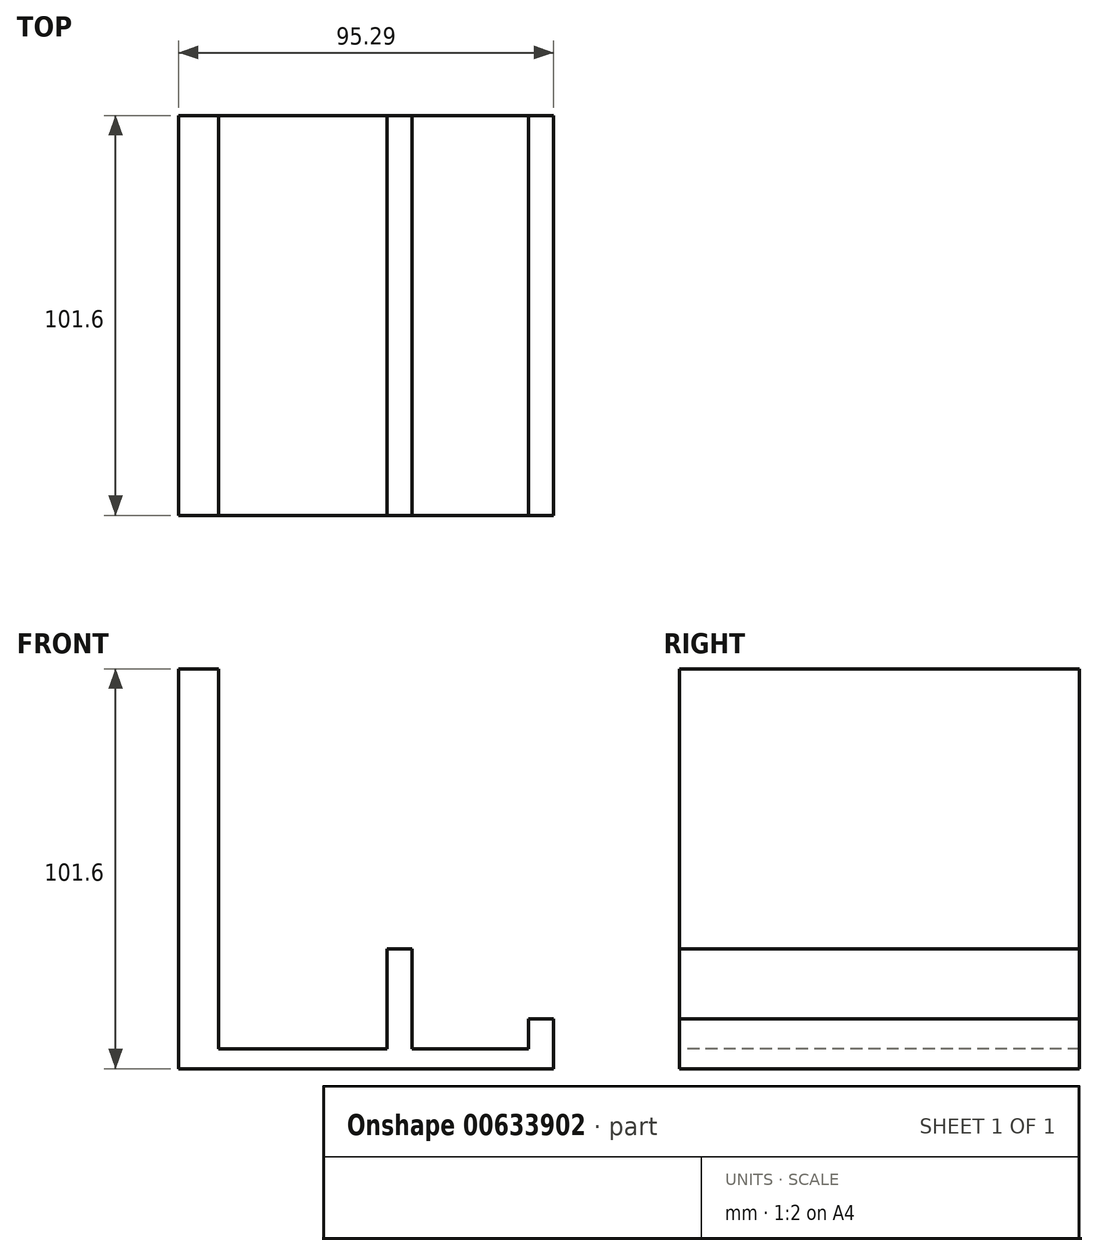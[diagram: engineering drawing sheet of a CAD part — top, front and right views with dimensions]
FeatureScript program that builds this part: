
annotation { "Feature Type Name" : "Feature", "Feature Type Description" : "" }
export const myFeature = defineFeature(function(context is Context, id is Id, definition is map)
    precondition{}
    {
        {
            var Q0;
            Q0=qCreatedBy(makeId("Front.planeOp"),FACE);
            var sketch = newSketch(context, id + "F0", { "sketchPlane" : qUnion([Q0])});
            skLineSegment(sketch, "E0", {"start": v(-57.6, 53.74) * mm, "end": v(-57.6, -47.86) * mm});
            skLineSegment(sketch, "E1", {"start": v(1.68, -42.78) * mm, "end": v(-47.46, -42.78) * mm});
            skLineSegment(sketch, "E2", {"start": v(-47.46, -42.78) * mm, "end": v(-47.46, 53.74) * mm});
            skLineSegment(sketch, "E3", {"start": v(-47.46, 53.74) * mm, "end": v(-57.6, 53.74) * mm});
            skLineSegment(sketch, "E4", {"start": v(-4.67, -42.78) * mm, "end": v(-4.67, -17.38) * mm});
            skLineSegment(sketch, "E5", {"start": v(-4.67, -17.38) * mm, "end": v(1.68, -17.38) * mm});
            skLineSegment(sketch, "E6", {"start": v(1.68, -17.38) * mm, "end": v(1.68, -42.78) * mm});
            skLineSegment(sketch, "E7", {"start": v(-57.6, -47.86) * mm, "end": v(37.7, -47.86) * mm});
            skLineSegment(sketch, "E8", {"start": v(37.7, -47.86) * mm, "end": v(37.7, -35.16) * mm});
            skLineSegment(sketch, "E9", {"start": v(37.7, -35.16) * mm, "end": v(31.34, -35.16) * mm});
            skLineSegment(sketch, "E10", {"start": v(31.34, -35.16) * mm, "end": v(31.34, -42.78) * mm});
            skLineSegment(sketch, "E11", {"start": v(31.34, -42.78) * mm, "end": v(1.68, -42.78) * mm});
            skSolve(sketch);
        }
        {
            var Q0;
            Q0=makeQuery(id+"F0.imprint","IMPRINT",FACE,{"disambiguationData":[TD([[makeQuery(id+"F0.imprint","IMPRINT",EDGE,{"derivedFrom":sQuery(id+"F0.wireOp",EDGE,"E0")}),1.0]])]});
            var Q1;
            {var subQ0=sQuery(id+"F0.wireOp",EDGE,"E4");Q1=makeQuery(id+"F0.imprint","IMPRINT",FACE,{"disambiguationData":[TD([[makeQuery(id+"F0.imprint","IMPRINT",EDGE,{"derivedFrom":subQ0}),-1.0]])]});}
            extrude(context, id + "F1", {"entities" : qUnion([Q0, Q1]), "oppositeDirection" : true, "depth" : 101.6 * mm, "offsetDistance" : 25.4 * mm});
        }
    });
